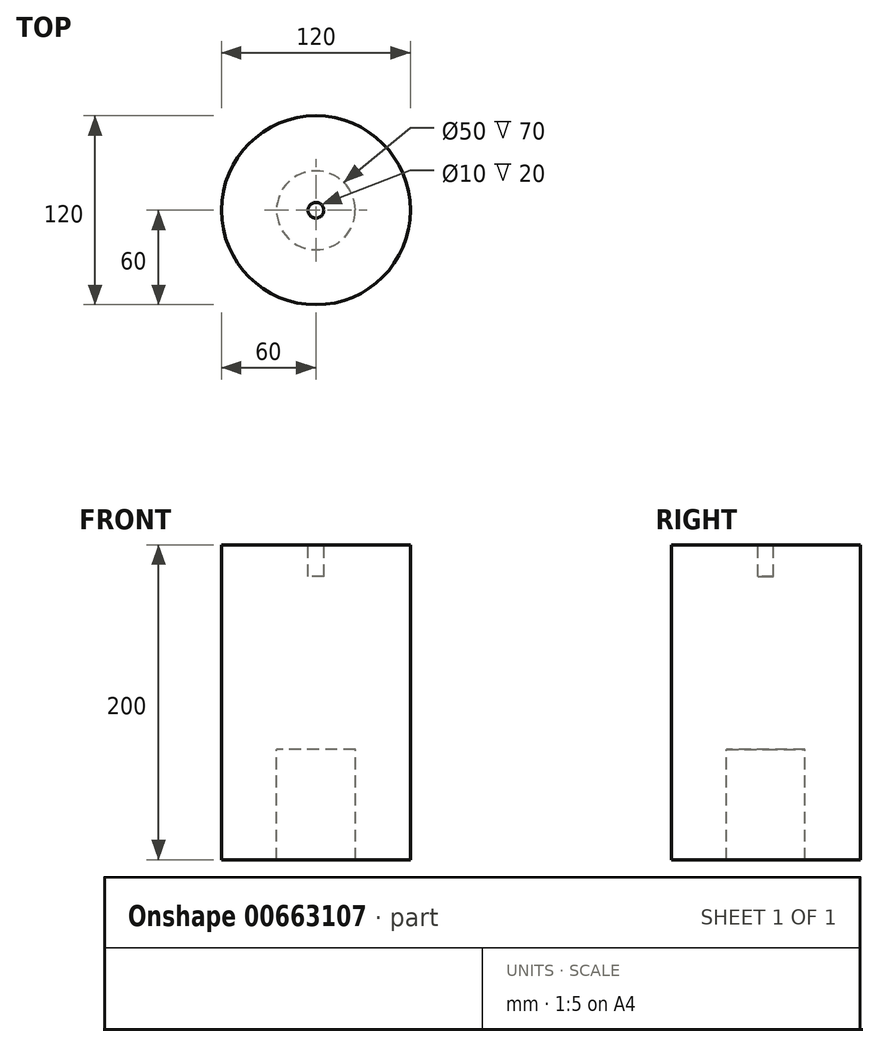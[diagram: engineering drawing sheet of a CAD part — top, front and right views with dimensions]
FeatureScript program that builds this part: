
annotation { "Feature Type Name" : "Feature", "Feature Type Description" : "" }
export const myFeature = defineFeature(function(context is Context, id is Id, definition is map)
    precondition{}
    {
        {
            var Q0;
            Q0=qCreatedBy(makeId("Front.planeOp"),FACE);
            var sketch = newSketch(context, id + "F0", { "sketchPlane" : qUnion([Q0])});
            skLineSegment(sketch, "E0", {"start": v(0, 0) * mm, "end": v(25, 0) * mm});
            skLineSegment(sketch, "E1", {"start": v(25, 0) * mm, "end": v(25, -70) * mm});
            skLineSegment(sketch, "E2", {"start": v(25, -70) * mm, "end": v(60, -70) * mm});
            skLineSegment(sketch, "E3", {"start": v(60, -70) * mm, "end": v(60, 130) * mm});
            skLineSegment(sketch, "E4", {"start": v(60, 130) * mm, "end": v(5, 130) * mm});
            skLineSegment(sketch, "E5", {"start": v(5, 130) * mm, "end": v(5, 110) * mm});
            skLineSegment(sketch, "E6", {"start": v(5, 110) * mm, "end": v(0, 110) * mm});
            skLineSegment(sketch, "E7", {"start": v(0, 110) * mm, "end": v(0, 0) * mm});
            skSolve(sketch);
        }
        {
            var Q0;
            Q0=makeQuery(id+"F0.imprint","IMPRINT",FACE,{"disambiguationData":[TD([[makeQuery(id+"F0.imprint","IMPRINT",EDGE,{"derivedFrom":sQuery(id+"F0.wireOp",EDGE,"E0")}),1.0]])]});
            var Q1;
            Q1=sQuery(id+"F0.wireOp",EDGE,"E7");
            revolve(context, id + "F1", {"entities" : qUnion([Q0]), "axis" : qUnion([Q1]), "revolveType" : RevolveType.FULL});
        }
    });
